annotation { "Feature Type Name" : "Feature", "Feature Type Description" : "" }
export const myFeature = defineFeature(function(context is Context, id is Id, definition is map)
    precondition{}
    {
        {
            var Q0;
            Q0=qCreatedBy(makeId("Top.planeOp"),FACE);
            var sketch = newSketch(context, id + "F0", { "sketchPlane" : qUnion([Q0])});
            skCircle(sketch, "E0", {"center": v(0, 0) * mm, "radius": 25 * mm});
            skText(sketch, "E1", { "text": "TIMON PROSPÈR", "fontName": "OpenSans-Bold.ttf"});
            skText(sketch, "E2", { "text": "+316 10 44 84 93", "fontName": "OpenSans-Regular.ttf"});
            skText(sketch, "E3", { "text": "<email>", "fontName": "OpenSans-Regular.ttf"});
            skText(sketch, "E4", { "text": "ART STUDENT\n", "fontName": "OpenSans-Regular.ttf"});
            skCircle(sketch, "E5", {"center": v(-5.22, 14.66) * mm, "radius": 2.83 * mm});
            skCircle(sketch, "E6", {"center": v(-3.48, 16.9) * mm, "radius": 1.96 * mm});
            skCircle(sketch, "E7", {"center": v(-2.4, 14.66) * mm, "radius": 2.98 * mm});
            skCircle(sketch, "E8", {"center": v(0.57, 14.3) * mm, "radius": 2.25 * mm});
            skCircle(sketch, "E9", {"center": v(2.65, 15.13) * mm, "radius": 1.64 * mm});
            skCircle(sketch, "E10", {"center": v(2.04, 16.65) * mm, "radius": 1.75 * mm});
            skCircle(sketch, "E11", {"center": v(-0.75, 17.15) * mm, "radius": 1.91 * mm});
            skCircle(sketch, "E12", {"center": v(4.24, 14.73) * mm, "radius": 2.68 * mm});
            const initialGuessF0  = {"E1": [-0.02424, 0, 1, 0, 0.00429], "E2": [-0.0175, -0.00676, 1, 0, 0.00319], "E3": [-0.0175, -0.0112, 1, 0, 0.00187], "E4": [-0.01, 0.0069, 1, 0, 0.0022]};
            skSetInitialGuess(sketch, initialGuessF0);
            skSolve(sketch);
        }
        {
            var Q0;
            Q0=qSketchRegion(id+"F0",true);
            extrude(context, id + "F1", {"entities" : qUnion([Q0]), "flatOperationType" : FlatOperationType.REMOVE, "depth" : 2 * mm, "offsetDistance" : 25 * mm, "domain" : OperationDomain.MODEL});
        }
    });